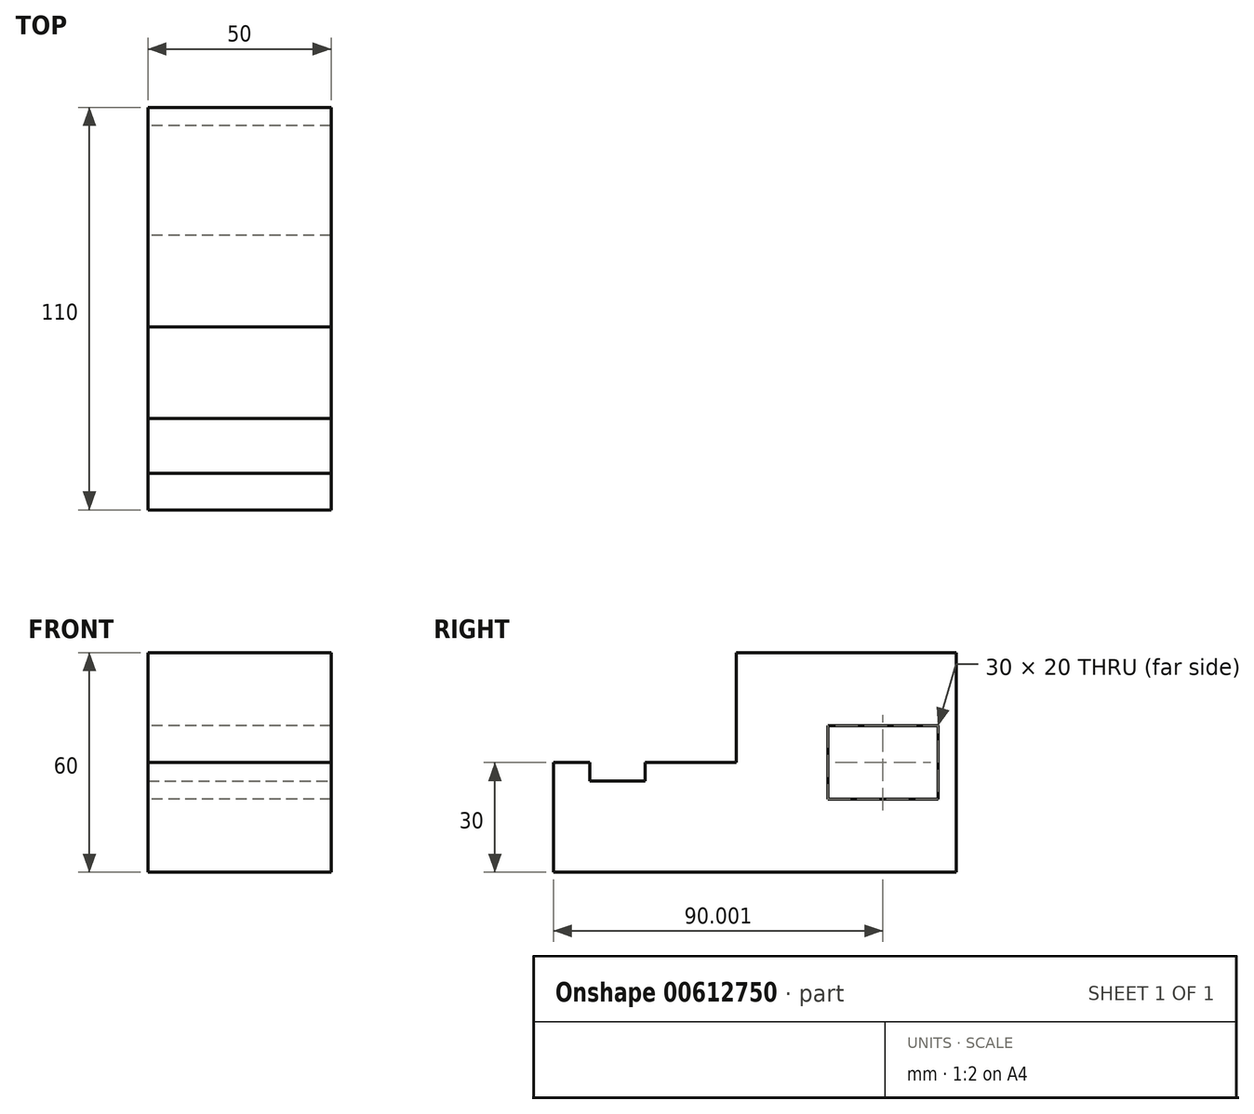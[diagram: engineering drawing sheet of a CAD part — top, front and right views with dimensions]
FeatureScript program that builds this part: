
annotation { "Feature Type Name" : "Feature", "Feature Type Description" : "" }
export const myFeature = defineFeature(function(context is Context, id is Id, definition is map)
    precondition{}
    {
        {
            var Q0;
            Q0=qCreatedBy(makeId("Top.planeOp"),FACE);
            var sketch = newSketch(context, id + "F0", { "sketchPlane" : qUnion([Q0])});
            skLineSegment(sketch, "E0.bottom", {"start": v(-21.46, 73.06) * mm, "end": v(28.54, 73.06) * mm});
            skLineSegment(sketch, "E0.top", {"start": v(-21.46, -36.94) * mm, "end": v(28.54, -36.94) * mm});
            skLineSegment(sketch, "E0.left", {"start": v(-21.46, 73.06) * mm, "end": v(-21.46, -36.94) * mm});
            skLineSegment(sketch, "E0.right", {"start": v(28.54, 73.06) * mm, "end": v(28.54, -36.94) * mm});
            skSolve(sketch);
        }
        {
            var Q0;
            Q0=makeQuery(id+"F0.imprint","IMPRINT",FACE,{"disambiguationData":[TD([[makeQuery(id+"F0.imprint","IMPRINT",EDGE,{"derivedFrom":sQuery(id+"F0.wireOp",EDGE,"E0.bottom")}),-1.0]])]});
            extrude(context, id + "F1", {"entities" : qUnion([Q0]), "depth" : 60 * mm, "offsetDistance" : 25 * mm});
        }
        {
            var Q0;
            Q0=makeQuery(id+"F1.opExtrude","CAP_FACE",FACE,{"disambiguationData":[OSD([sQuery(id+"F0.wireOp",EDGE,"E0.bottom"),sQuery(id+"F0.wireOp",EDGE,"E0.top"),sQuery(id+"F0.wireOp",EDGE,"E0.left"),sQuery(id+"F0.wireOp",EDGE,"E0.right")])],"isStart":false});
            var sketch = newSketch(context, id + "F2", { "sketchPlane" : qUnion([Q0])});
            skLineSegment(sketch, "E1", {"start": v(-21.46, 73.06) * mm, "end": v(-21.46, 13.06) * mm});
            skLineSegment(sketch, "E2", {"start": v(-21.46, 13.06) * mm, "end": v(28.54, 13.06) * mm});
            skSolve(sketch);
        }
        {
            var Q0;
            {var subQ0=sQuery(id+"F2.wireOp",EDGE,"E2");Q0=makeQuery(id+"F2.imprint","IMPRINT",FACE,{"disambiguationData":[TD([[makeQuery(id+"F2.imprint","IMPRINT",EDGE,{"derivedFrom":subQ0}),-1.0]])]});}
            extrude(context, id + "F3", {"entities" : qUnion([Q0]), "operationType" : NewBodyOperationType.REMOVE, "oppositeDirection" : true, "depth" : 30 * mm, "offsetDistance" : 25 * mm});
        }
        {
            var Q0;
            Q0=makeQuery(id+"F3.boolean.opBoolean","COPY",FACE,{"derivedFrom":makeQuery(id+"F3.opExtrude","CAP_FACE",FACE,{"disambiguationData":[OSD([sQuery(id+"F0.wireOp",EDGE,"E0.top"),sQuery(id+"F0.wireOp",EDGE,"E0.left"),sQuery(id+"F0.wireOp",EDGE,"E0.right"),sQuery(id+"F2.wireOp",EDGE,"E2")])],"isStart":false})});
            var sketch = newSketch(context, id + "F4", { "sketchPlane" : qUnion([Q0])});
            skLineSegment(sketch, "E3", {"start": v(-21.46, -36.94) * mm, "end": v(-21.46, -26.94) * mm});
            skLineSegment(sketch, "E4", {"start": v(-21.46, -26.94) * mm, "end": v(28.54, -26.94) * mm});
            skLineSegment(sketch, "E5", {"start": v(28.54, -26.94) * mm, "end": v(28.54, -11.94) * mm});
            skLineSegment(sketch, "E6", {"start": v(28.54, -11.94) * mm, "end": v(-21.46, -11.94) * mm});
            skLineSegment(sketch, "E7", {"start": v(-21.46, -11.94) * mm, "end": v(-21.46, -26.94) * mm});
            skSolve(sketch);
        }
        {
            var Q0;
            Q0=makeQuery(id+"F4.imprint","IMPRINT",FACE,{"disambiguationData":[TD([[makeQuery(id+"F4.imprint","IMPRINT",EDGE,{"derivedFrom":sQuery(id+"F4.wireOp",EDGE,"E4")}),1.0]])]});
            extrude(context, id + "F5", {"entities" : qUnion([Q0]), "operationType" : NewBodyOperationType.REMOVE, "oppositeDirection" : true, "depth" : 5 * mm, "offsetDistance" : 25 * mm});
        }
        {
            var Q0;
            Q0=makeQuery(id+"F1.opExtrude","SWEPT_FACE",FACE,{"disambiguationData":[OSD([sQuery(id+"F0.wireOp",EDGE,"E0.left")])]});
            var sketch = newSketch(context, id + "F6", { "sketchPlane" : qUnion([Q0])});
            skLineSegment(sketch, "E8", {"start": v(-73.06, 0) * mm, "end": v(-73.06, 20) * mm});
            skLineSegment(sketch, "E9", {"start": v(-73.06, 20) * mm, "end": v(7.37, 20) * mm});
            skLineSegment(sketch, "E10", {"start": v(-73.06, 60) * mm, "end": v(-73.06, 40) * mm});
            skLineSegment(sketch, "E11", {"start": v(-73.06, 40) * mm, "end": v(-13.06, 40) * mm});
            skLineSegment(sketch, "E12", {"start": v(-73.06, 40) * mm, "end": v(-68.06, 40) * mm});
            skLineSegment(sketch, "E13", {"start": v(-68.06, 40) * mm, "end": v(-68.06, 20) * mm});
            skLineSegment(sketch, "E14", {"start": v(-68.06, 20) * mm, "end": v(-38.06, 20) * mm});
            skLineSegment(sketch, "E15", {"start": v(-38.06, 20) * mm, "end": v(-38.06, 40) * mm});
            skSolve(sketch);
        }
        {
            var Q0;
            {var subQ0=sQuery(id+"F6.wireOp",EDGE,"E13");Q0=makeQuery(id+"F6.imprint","IMPRINT",FACE,{"disambiguationData":[TD([[makeQuery(id+"F6.imprint","IMPRINT",EDGE,{"derivedFrom":subQ0}),1.0]])]});}
            extrude(context, id + "F7", {"entities" : qUnion([Q0]), "operationType" : NewBodyOperationType.REMOVE, "oppositeDirection" : true, "depth" : 92 * mm, "offsetDistance" : 25 * mm});
        }
    });
